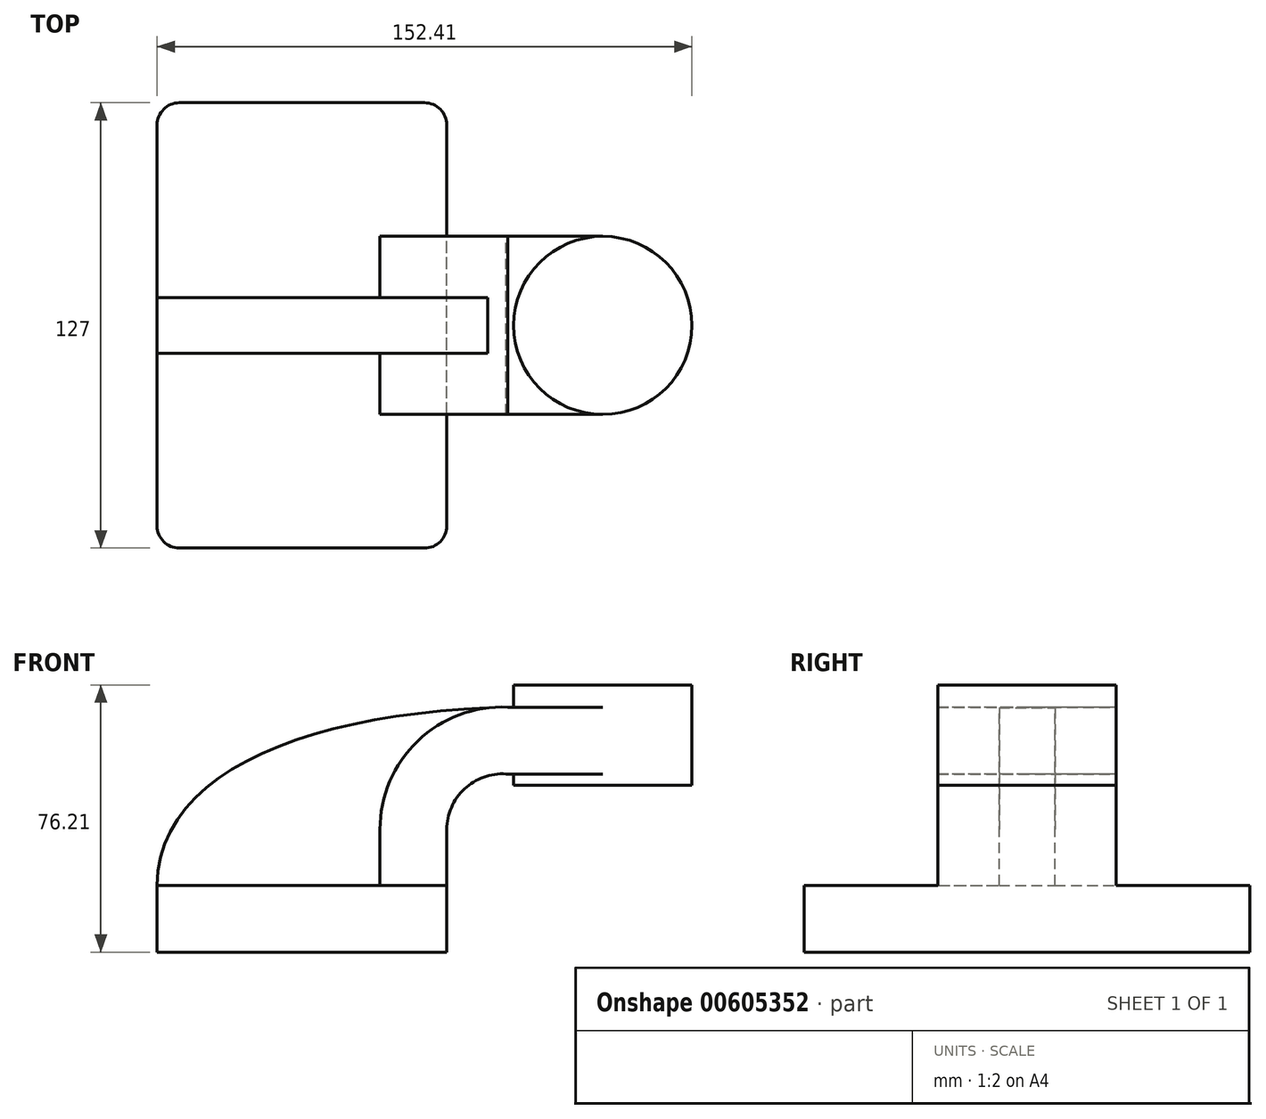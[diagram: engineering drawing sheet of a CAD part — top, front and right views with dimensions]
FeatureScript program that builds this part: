
annotation { "Feature Type Name" : "Feature", "Feature Type Description" : "" }
export const myFeature = defineFeature(function(context is Context, id is Id, definition is map)
    precondition{}
    {
        {
            var Q0;
            Q0=qCreatedBy(makeId("Front.planeOp"),FACE);
            var sketch = newSketch(context, id + "F0", { "sketchPlane" : qUnion([Q0])});
            skLineSegment(sketch, "E0.bottom", {"start": v(-41.28, -9.53) * mm, "end": v(41.28, -9.53) * mm});
            skLineSegment(sketch, "E0.top", {"start": v(-41.28, 9.52) * mm, "end": v(41.28, 9.52) * mm});
            skLineSegment(sketch, "E0.left", {"start": v(-41.28, -9.53) * mm, "end": v(-41.28, 9.52) * mm});
            skLineSegment(sketch, "E0.right", {"start": v(41.28, -9.53) * mm, "end": v(41.28, 9.52) * mm});
            skPoint(sketch, "E0.middle", {"position": v(0, 0) * mm});
            skLineSegment(sketch, "E1.bottom", {"start": v(60.32, 38.1) * mm, "end": v(111.12, 38.1) * mm});
            skLineSegment(sketch, "E1.top", {"start": v(60.32, 66.67) * mm, "end": v(111.12, 66.67) * mm});
            skLineSegment(sketch, "E1.left", {"start": v(60.32, 38.1) * mm, "end": v(60.32, 66.67) * mm});
            skLineSegment(sketch, "E1.right", {"start": v(111.12, 38.1) * mm, "end": v(111.12, 66.67) * mm});
            skPoint(sketch, "E1.middle", {"position": v(85.72, 52.39) * mm});
            skLineSegment(sketch, "E2", {"start": v(41.27, 9.52) * mm, "end": v(41.27, 25.43) * mm});
            skArc(sketch, "E3", {"start": v(41.27, 25.43) * mm, "mid": v(46.29, 37) * mm, "end": v(58.16, 41.27) * mm});
            skLineSegment(sketch, "E4", {"start": v(58.16, 41.27) * mm, "end": v(85.72, 41.27) * mm});
            skFitSpline(sketch, "E5", {"points": [v(-41.28, 9.53) * mm, v(59.37, 60.29) * mm], "startDerivative": vector(1.16, 100.22) * mm, "endDerivative": vector(165.85, 3) * mm});
            skLineSegment(sketch, "E6.0", {"start": v(58.65, 60.32) * mm, "end": v(85.72, 60.32) * mm});
            skArc(sketch, "E6.1", {"start": v(22.23, 25.43) * mm, "mid": v(32.99, 50.65) * mm, "end": v(58.65, 60.32) * mm});
            skLineSegment(sketch, "E6.2", {"start": v(22.23, 9.52) * mm, "end": v(22.23, 25.43) * mm});
            skLineSegment(sketch, "E7", {"start": v(85.72, 38.1) * mm, "end": v(85.72, 66.67) * mm});
            skSolve(sketch);
        }
        {
            var Q0;
            Q0=makeQuery(id+"F0.imprint","IMPRINT",FACE,{"disambiguationData":[TD([[makeQuery(id+"F0.imprint","IMPRINT",EDGE,{"derivedFrom":sQuery(id+"F0.wireOp",EDGE,"E0.bottom")}),1.0]])]});
            extrude(context, id + "F1", {"entities" : qUnion([Q0]), "endBound" : BoundingType.SYMMETRIC, "depth" : 127 * mm, "offsetDistance" : 25.4 * mm});
        }
        {
            var Q0;
            {var subQ0=sQuery(id+"F0.wireOp",EDGE,"E2");Q0=makeQuery(id+"F0.imprint","IMPRINT",FACE,{"disambiguationData":[TD([[makeQuery(id+"F0.imprint","IMPRINT",EDGE,{"derivedFrom":subQ0}),1.0]])]});}
            extrude(context, id + "F2", {"entities" : qUnion([Q0]), "operationType" : NewBodyOperationType.ADD, "endBound" : BoundingType.SYMMETRIC, "depth" : 50.8 * mm, "offsetDistance" : 25.4 * mm});
        }
        {
            var Q0;
            {var subQ3=sQuery(id+"F0.wireOp",EDGE,"E6.2");Q0=makeQuery(id+"F0.imprint","IMPRINT",FACE,{"disambiguationData":[TD([[makeQuery(id+"F0.imprint","IMPRINT",EDGE,{"derivedFrom":subQ3}),1.0]])]});}
            extrude(context, id + "F3", {"entities" : qUnion([Q0]), "operationType" : NewBodyOperationType.ADD, "endBound" : BoundingType.SYMMETRIC, "depth" : 15.88 * mm, "offsetDistance" : 25.4 * mm});
        }
        {
            var Q0;
            {var subQ0=sQuery(id+"F0.wireOp",EDGE,"E4");var subQ1=sQuery(id+"F0.wireOp",EDGE,"E1.left");var subQ2=makeQuery(id+"F0.imprint","INTERSECT",VERTEX,{"derivedFrom":[subQ1,subQ0]});Q0=makeQuery(id+"F0.imprint","IMPRINT",FACE,{"disambiguationData":[TD([[makeQuery(id+"F0.imprint","IMPRINT",EDGE,{"disambiguationData":[TD([[subQ2,-1.0]])],"derivedFrom":subQ1}),-1.0]])]});}
            extrude(context, id + "F4", {"entities" : qUnion([Q0]), "operationType" : NewBodyOperationType.ADD, "endBound" : BoundingType.SYMMETRIC, "depth" : 50.8 * mm, "offsetDistance" : 25.4 * mm});
        }
        {
            var Q0;
            {var subQ0=sQuery(id+"F0.wireOp",EDGE,"E1.right");Q0=makeQuery(id+"F0.imprint","IMPRINT",FACE,{"disambiguationData":[TD([[makeQuery(id+"F0.imprint","IMPRINT",EDGE,{"derivedFrom":subQ0}),1.0]])]});}
            var Q1;
            Q1=sQuery(id+"F0.wireOp",EDGE,"E7");
            revolve(context, id + "F5", {"operationType" : NewBodyOperationType.ADD, "entities" : qUnion([Q0]), "axis" : qUnion([Q1]), "revolveType" : RevolveType.FULL});
        }
        {
            var Q0;
            Q0=makeQuery(id+"F1.opExtrude","CAP_EDGE",EDGE,{"disambiguationData":[OSD([sQuery(id+"F0.wireOp",EDGE,"E0.left")])],"isStart":false});
            var Q1;
            Q1=makeQuery(id+"F1.opExtrude","CAP_EDGE",EDGE,{"disambiguationData":[OSD([sQuery(id+"F0.wireOp",EDGE,"E0.right")])],"isStart":false});
            var Q2;
            Q2=makeQuery(id+"F1.opExtrude","CAP_EDGE",EDGE,{"disambiguationData":[OSD([sQuery(id+"F0.wireOp",EDGE,"E0.right")])],"isStart":true});
            var Q3;
            Q3=makeQuery(id+"F1.opExtrude","CAP_EDGE",EDGE,{"disambiguationData":[OSD([sQuery(id+"F0.wireOp",EDGE,"E0.left")])],"isStart":true});
            fillet(context, id + "F6", {"entities" : qUnion([Q0, Q1, Q2, Q3]), "radius" : 6.35 * mm, "tangentPropagation" : true, "allowEdgeOverflow" : false});
        }
    });
